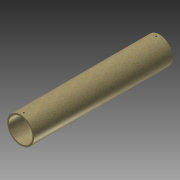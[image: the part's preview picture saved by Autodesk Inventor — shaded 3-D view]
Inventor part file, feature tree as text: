
AUTODESK INVENTOR PART (.ipt)
format: ipt  version: 2012 (Build 160160000, 160)  size: 100,864 bytes
history: native  units: in
note: dims shown in document units (in); Inventor stores cm internally (conversion verified against a paired STEP export)
features: extrude x2, sketch x2
ambient origin geometry x8: Origin, YZ Plane, XZ Plane, XY Plane, X Axis, Y Axis, Z Axis, Center Point
bodies: Solid1 (feature_tree)
feature tree (4):
  extrude  "Extrusion1"  Depth=2.125in
  extrude  "Extrusion2"  Depth=0.25in
  sketch  "Sketch1"  dims[d0=1.875in d1=2.125in]
  sketch  "Sketch2"  dims[d2=11.0in d3=0.0in d4=0.25in d5=0.25in d6=0.136in d7=1.0in d8=0.0in]
